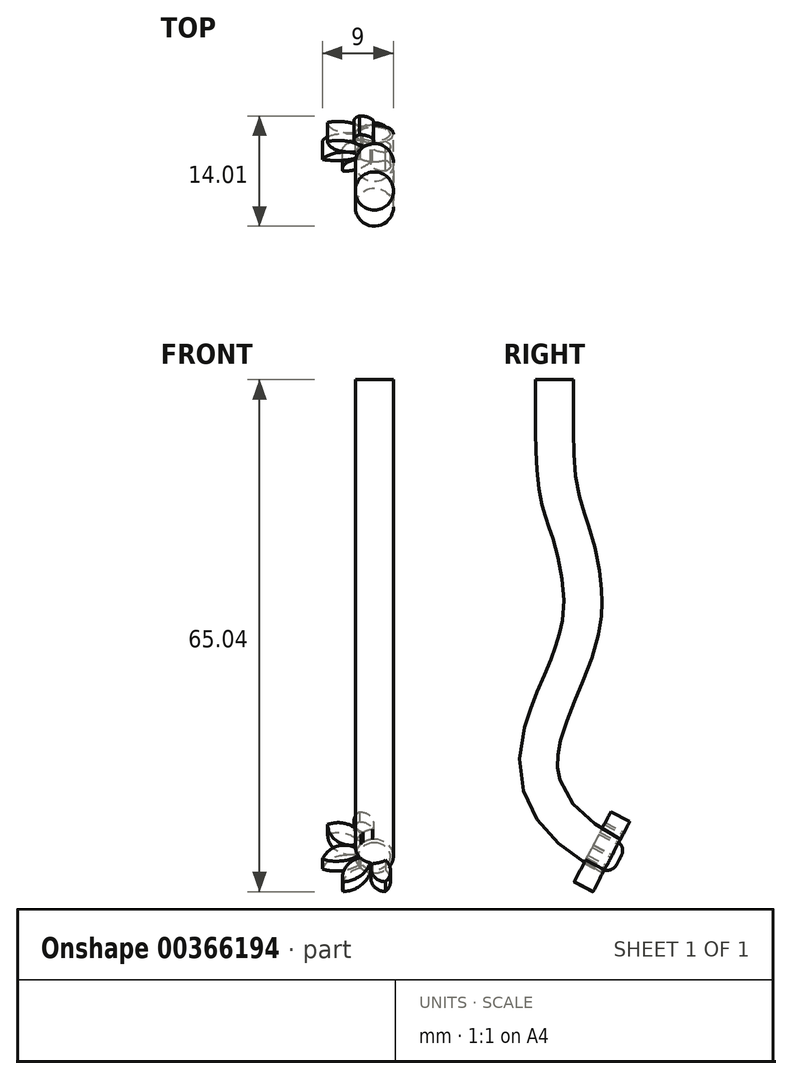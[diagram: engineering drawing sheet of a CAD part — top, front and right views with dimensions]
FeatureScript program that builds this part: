
annotation { "Feature Type Name" : "Feature", "Feature Type Description" : "" }
export const myFeature = defineFeature(function(context is Context, id is Id, definition is map)
    precondition{}
    {
        {
            var Q0;
            Q0=qCreatedBy(makeId("Top.planeOp"),FACE);
            var sketch = newSketch(context, id + "F0", { "sketchPlane" : qUnion([Q0])});
            skCircle(sketch, "E0", {"center": v(0, 0) * mm, "radius": 2.42 * mm});
            skSolve(sketch);
        }
        {
            var Q0;
            Q0=qCreatedBy(makeId("Right.planeOp"),FACE);
            var sketch = newSketch(context, id + "F1", { "sketchPlane" : qUnion([Q0])});
            skLineSegment(sketch, "E1", {"start": v(0, 0) * mm, "end": v(0, -6.62) * mm});
            skFitSpline(sketch, "E2", {"points": [v(0, -6.62) * mm, v(1.96, -19.05) * mm, v(3.47, -30.46) * mm, v(-0.87, -42.92) * mm, v(7.25, -60.53) * mm], "startDerivative": vector(0, -97.45) * mm, "endDerivative": vector(111.72, -58.44) * mm});
            skSolve(sketch);
        }
        {
            var Q0;
            Q0=makeQuery(id+"F0.imprint","IMPRINT",FACE,{"disambiguationData":[TD([[makeQuery(id+"F0.imprint","IMPRINT",EDGE,{"derivedFrom":sQuery(id+"F0.wireOp",EDGE,"E0")}),1.0]])]});
            var Q1;
            Q1=sQuery(id+"F1.wireOp",EDGE,"E1");
            var Q2;
            Q2=sQuery(id+"F1.wireOp",EDGE,"E2");
            sweep(context, id + "F2", {"profiles" : qUnion([Q0]), "path" : qUnion([Q1, Q2])});
        }
        {
            var Q0;
            Q0=makeQuery(id+"F2.opSweep","CAP_FACE",FACE,{"disambiguationData":[OSD([sQuery(id+"F0.wireOp",EDGE,"E0"),sQuery(id+"F1.wireOp",VERTEX,"E2.end")])],"isStart":false});
            var sketch = newSketch(context, id + "F3", { "sketchPlane" : qUnion([Q0])});
            skCircle(sketch, "E3", {"center": v(0, -50.28) * mm, "radius": 1.99 * mm});
            skSolve(sketch);
        }
        {
            var Q0;
            Q0=makeQuery(id+"F3.imprint","IMPRINT",FACE,{"disambiguationData":[TD([[makeQuery(id+"F3.imprint","IMPRINT",EDGE,{"derivedFrom":sQuery(id+"F3.wireOp",EDGE,"E3")}),1.0]])]});
            extrude(context, id + "F4", {"entities" : qUnion([Q0]), "operationType" : NewBodyOperationType.ADD, "depth" : 1.07 * mm, "offsetDistance" : 25 * mm});
        }
        {
            var Q0;
            Q0=makeQuery(id+"F4.opExtrude","CAP_FACE",FACE,{"disambiguationData":[OSD([sQuery(id+"F3.wireOp",EDGE,"E3")])],"isStart":false});
            fillet(context, id + "F5", {"entities" : qUnion([Q0]), "radius" : 1.4 * mm, "tangentPropagation" : true, "allowEdgeOverflow" : false});
        }
        {
            var Q0;
            Q0=makeQuery(id+"F2.opSweep","CAP_FACE",FACE,{"disambiguationData":[OSD([sQuery(id+"F0.wireOp",EDGE,"E0"),sQuery(id+"F1.wireOp",VERTEX,"E2.end")])],"isStart":false});
            var sketch = newSketch(context, id + "F6", { "sketchPlane" : qUnion([Q0])});
            skArc(sketch, "E4", {"start": v(3.98, -55.37) * mm, "mid": v(3.6, -53.18) * mm, "end": v(1.78, -51.93) * mm});
            skArc(sketch, "E5", {"start": v(0.5, -52.65) * mm, "mid": v(1.82, -54.55) * mm, "end": v(3.98, -55.37) * mm});
            skArc(sketch, "E6", {"start": v(2.02, -51.62) * mm, "mid": v(4.24, -52.4) * mm, "end": v(6.58, -52.12) * mm});
            skArc(sketch, "E7", {"start": v(6.58, -52.12) * mm, "mid": v(4.88, -50.33) * mm, "end": v(2.42, -50.44) * mm});
            skArc(sketch, "E8", {"start": v(2.41, -50.06) * mm, "mid": v(4.86, -49.44) * mm, "end": v(5.93, -47.16) * mm});
            skArc(sketch, "E9", {"start": v(5.93, -47.16) * mm, "mid": v(3.55, -47.05) * mm, "end": v(1.7, -48.56) * mm});
            skArc(sketch, "E10.MirrorCS", {"start": v(-5.93, -52.24) * mm, "mid": v(-4.5, -50.71) * mm, "end": v(-2.4, -50.58) * mm});
            skArc(sketch, "E11.MirrorCS", {"start": v(-1.6, -52.1) * mm, "mid": v(-3.74, -52.83) * mm, "end": v(-5.93, -52.24) * mm});
            skArc(sketch, "E12.MirrorCS", {"start": v(-6.2, -48.1) * mm, "mid": v(-3.92, -47.6) * mm, "end": v(-2, -48.9) * mm});
            skArc(sketch, "E13.MirrorCS", {"start": v(-2.42, -50.28) * mm, "mid": v(-4.54, -49.6) * mm, "end": v(-6.2, -48.1) * mm});
            skArc(sketch, "E14.MirrorCS", {"start": v(-1.83, -48.69) * mm, "mid": v(-3.28, -46.77) * mm, "end": v(-2.82, -44.4) * mm});
            skArc(sketch, "E15.MirrorCS", {"start": v(-2.82, -44.4) * mm, "mid": v(-0.83, -45.63) * mm, "end": v(-0.15, -47.86) * mm});
            skArc(sketch, "E16", {"start": v(-1.4, -55.35) * mm, "mid": v(0.15, -54.47) * mm, "end": v(0.26, -52.69) * mm});
            skArc(sketch, "E17", {"start": v(-1.4, -52.25) * mm, "mid": v(-2.06, -53.8) * mm, "end": v(-1.4, -55.35) * mm});
            skArc(sketch, "E18", {"start": v(1.42, -48.32) * mm, "mid": v(2.57, -46.97) * mm, "end": v(1.92, -45.33) * mm});
            skArc(sketch, "E19", {"start": v(1.92, -45.33) * mm, "mid": v(0.39, -46.14) * mm, "end": v(0.25, -47.87) * mm});
            skSolve(sketch);
        }
        {
            var Q0;
            {var subQ0=sQuery(id+"F6.wireOp",EDGE,"E8");Q0=makeQuery(id+"F6.imprint","IMPRINT",FACE,{"disambiguationData":[TD([[makeQuery(id+"F6.imprint","IMPRINT",EDGE,{"derivedFrom":subQ0}),1.0]])]});}
            var Q1;
            {var subQ0=sQuery(id+"F6.wireOp",EDGE,"E6");Q1=makeQuery(id+"F6.imprint","IMPRINT",FACE,{"disambiguationData":[TD([[makeQuery(id+"F6.imprint","IMPRINT",EDGE,{"derivedFrom":subQ0}),1.0]])]});}
            var Q2;
            {var subQ0=sQuery(id+"F6.wireOp",EDGE,"E4");Q2=makeQuery(id+"F6.imprint","IMPRINT",FACE,{"disambiguationData":[TD([[makeQuery(id+"F6.imprint","IMPRINT",EDGE,{"derivedFrom":subQ0}),1.0]])]});}
            var Q3;
            {var subQ0=sQuery(id+"F6.wireOp",EDGE,"E16");Q3=makeQuery(id+"F6.imprint","IMPRINT",FACE,{"disambiguationData":[TD([[makeQuery(id+"F6.imprint","IMPRINT",EDGE,{"derivedFrom":subQ0}),1.0]])]});}
            var Q4;
            {var subQ0=sQuery(id+"F6.wireOp",EDGE,"E10.MirrorCS");Q4=makeQuery(id+"F6.imprint","IMPRINT",FACE,{"disambiguationData":[TD([[makeQuery(id+"F6.imprint","IMPRINT",EDGE,{"derivedFrom":subQ0}),-1.0]])]});}
            var Q5;
            {var subQ0=sQuery(id+"F6.wireOp",EDGE,"E12.MirrorCS");Q5=makeQuery(id+"F6.imprint","IMPRINT",FACE,{"disambiguationData":[TD([[makeQuery(id+"F6.imprint","IMPRINT",EDGE,{"derivedFrom":subQ0}),-1.0]])]});}
            var Q6;
            {var subQ0=sQuery(id+"F6.wireOp",EDGE,"E14.MirrorCS");Q6=makeQuery(id+"F6.imprint","IMPRINT",FACE,{"disambiguationData":[TD([[makeQuery(id+"F6.imprint","IMPRINT",EDGE,{"derivedFrom":subQ0}),-1.0]])]});}
            var Q7;
            {var subQ0=sQuery(id+"F6.wireOp",EDGE,"E18");Q7=makeQuery(id+"F6.imprint","IMPRINT",FACE,{"disambiguationData":[TD([[makeQuery(id+"F6.imprint","IMPRINT",EDGE,{"derivedFrom":subQ0}),1.0]])]});}
            extrude(context, id + "F7", {"entities" : qUnion([Q0, Q1, Q2, Q3, Q4, Q5, Q6, Q7]), "oppositeDirection" : true, "depth" : 2.7 * mm, "offsetDistance" : 25 * mm});
        }
    });
